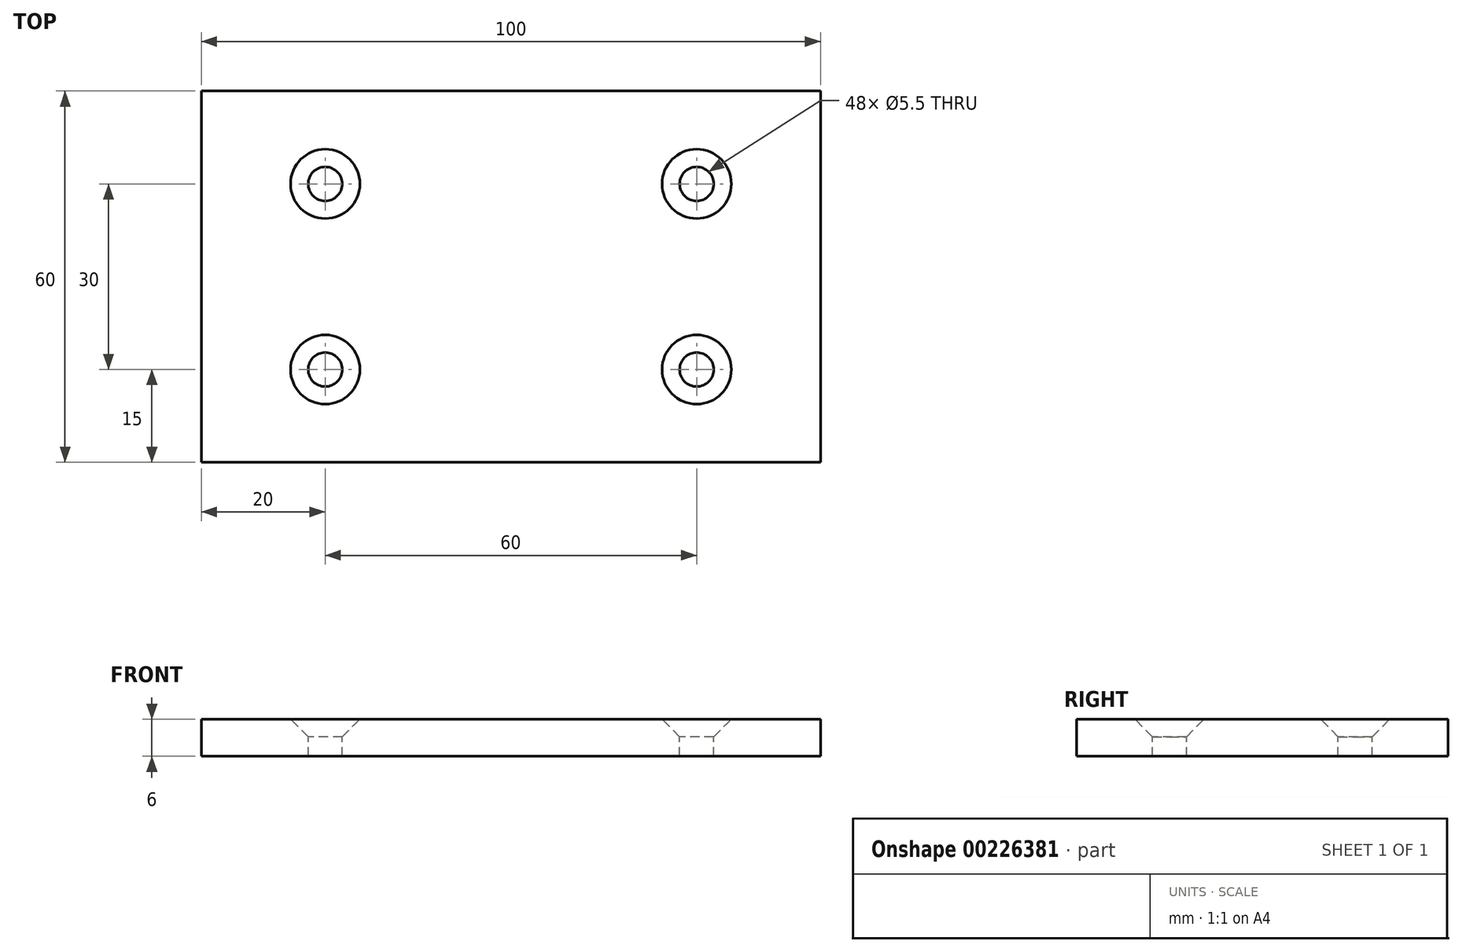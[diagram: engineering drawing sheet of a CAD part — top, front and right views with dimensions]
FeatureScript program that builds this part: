
annotation { "Feature Type Name" : "Feature", "Feature Type Description" : "" }
export const myFeature = defineFeature(function(context is Context, id is Id, definition is map)
    precondition{}
    {
        {
            var Q0;
            Q0=qCreatedBy(makeId("Top.planeOp"),FACE);
            var sketch = newSketch(context, id + "F0", { "sketchPlane" : qUnion([Q0])});
            skLineSegment(sketch, "E0.bottom", {"start": v(50, -30) * mm, "end": v(-50, -30) * mm});
            skLineSegment(sketch, "E0.top", {"start": v(50, 30) * mm, "end": v(-50, 30) * mm});
            skLineSegment(sketch, "E0.left", {"start": v(50, -30) * mm, "end": v(50, 30) * mm});
            skLineSegment(sketch, "E0.right", {"start": v(-50, -30) * mm, "end": v(-50, 30) * mm});
            skPoint(sketch, "E0.middle", {"position": v(0, 0) * mm});
            skSolve(sketch);
        }
        {
            var Q0;
            Q0=makeQuery(id+"F0.imprint","IMPRINT",FACE,{"disambiguationData":[TD([[makeQuery(id+"F0.imprint","IMPRINT",EDGE,{"derivedFrom":sQuery(id+"F0.wireOp",EDGE,"E0.bottom")}),-1.0]])]});
            extrude(context, id + "F1", {"entities" : qUnion([Q0]), "depth" : 6 * mm});
        }
        {
            var Q0;
            Q0=makeQuery(id+"F1.opExtrude","CAP_FACE",FACE,{"disambiguationData":[OSD([sQuery(id+"F0.wireOp",EDGE,"E0.bottom"),sQuery(id+"F0.wireOp",EDGE,"E0.top"),sQuery(id+"F0.wireOp",EDGE,"E0.left"),sQuery(id+"F0.wireOp",EDGE,"E0.right")])],"isStart":false});
            var sketch = newSketch(context, id + "F2", { "sketchPlane" : qUnion([Q0])});
            skPoint(sketch, "E1", {"position": v(-30, 15) * mm});
            skPoint(sketch, "E2", {"position": v(-30, -15) * mm});
            skPoint(sketch, "E3", {"position": v(30, -15) * mm});
            skPoint(sketch, "E4", {"position": v(30, 15) * mm});
            skSolve(sketch);
        }
        {
            var Q0;
            Q0=sQuery(id+"F2.wireOp",VERTEX,"E2");
            var Q1;
            Q1=sQuery(id+"F2.wireOp",VERTEX,"E1");
            var Q2;
            Q2=sQuery(id+"F2.wireOp",VERTEX,"E3");
            var Q3;
            Q3=sQuery(id+"F2.wireOp",VERTEX,"E4");
            var Q4;
            Q4=makeQuery(id+"F1.opExtrude","SWEPT_BODY",BODY,{"disambiguationData":[OSD([sQuery(id+"F0.wireOp",EDGE,"E0.bottom"),sQuery(id+"F0.wireOp",EDGE,"E0.top"),sQuery(id+"F0.wireOp",EDGE,"E0.left"),sQuery(id+"F0.wireOp",EDGE,"E0.right")])]});
            hole(context, id + "F3", {"style" : HoleStyle.C_SINK, "endStyle" : HoleEndStyle.THROUGH, "standardTappedOrClearance" : lookupTablePath({ "standard" : "ISO", "fit" : "Normal", "size" : "M5", "type" : "Clearance" }), "standardBlindInLast" : lookupTablePath({ "fit" : "Standard", "standard" : "ISO", "size" : "M5", "type" : "Clearance" }), "holeDiameter" : 5.5 * mm, "cSinkDiameter" : 11.2 * mm, "cSinkAngle" : 90 * degree, "locations" : qUnion([Q0, Q1, Q2, Q3]), "scope" : qUnion([Q4]), "isTappedThrough" : true});
        }
    });
